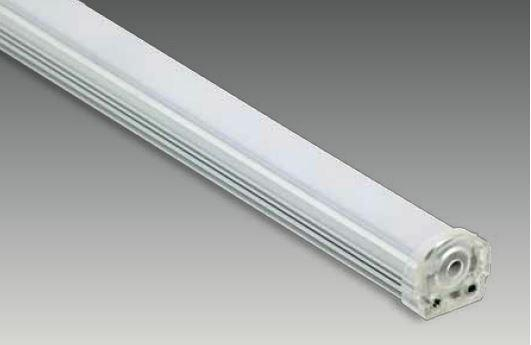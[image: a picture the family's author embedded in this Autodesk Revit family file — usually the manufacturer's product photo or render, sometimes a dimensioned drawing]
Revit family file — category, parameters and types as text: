
# Revit family: SD 1495 CVI
name_source: partatom
category: Lighting Fixtures
revit_build: Autodesk Revit 2017 (Build: 20160225_1515(x64)
units: mm (PartAtom-declared; Revit-internal decimal feet)

## family parameters
Cut with Voids When Loaded = No
Host = Face
Light Source = Yes
Part Type = Normal
Room Calculation Point = No
Round Connector Dimension = Use Diameter
Shared = No

## types (2) — shared parameters
Apparent Load = 24 VA
Color Filter = 16777215
Default Elevation = 1219 mm
Dimming Lamp Color Temperature Shift = <None>
Emit Shape Visible in Rendering = Yes
Emit from Rectangle Length = 15 mm  [stored 0.0492126 ft]
Emit from Rectangle Width = 1490 mm  [stored 4.88845 ft]
Light Source Symbol Size = 610 mm
Manufacturer = ARLIGHT
Type Image = SD 1495 CVI.JPG
Wattage Comments = 24

## type names (no varying parameters)
- SDCVI.1495.24.30
- SDCVI.1495.24.40

note: [stored X ft] marks values corroborated as IEEE doubles in the binary element streams (Revit-internal decimal feet)

## geometry (parser evidence)
native form markers: Sweep x3
no freeform markers — native parametric forms only
